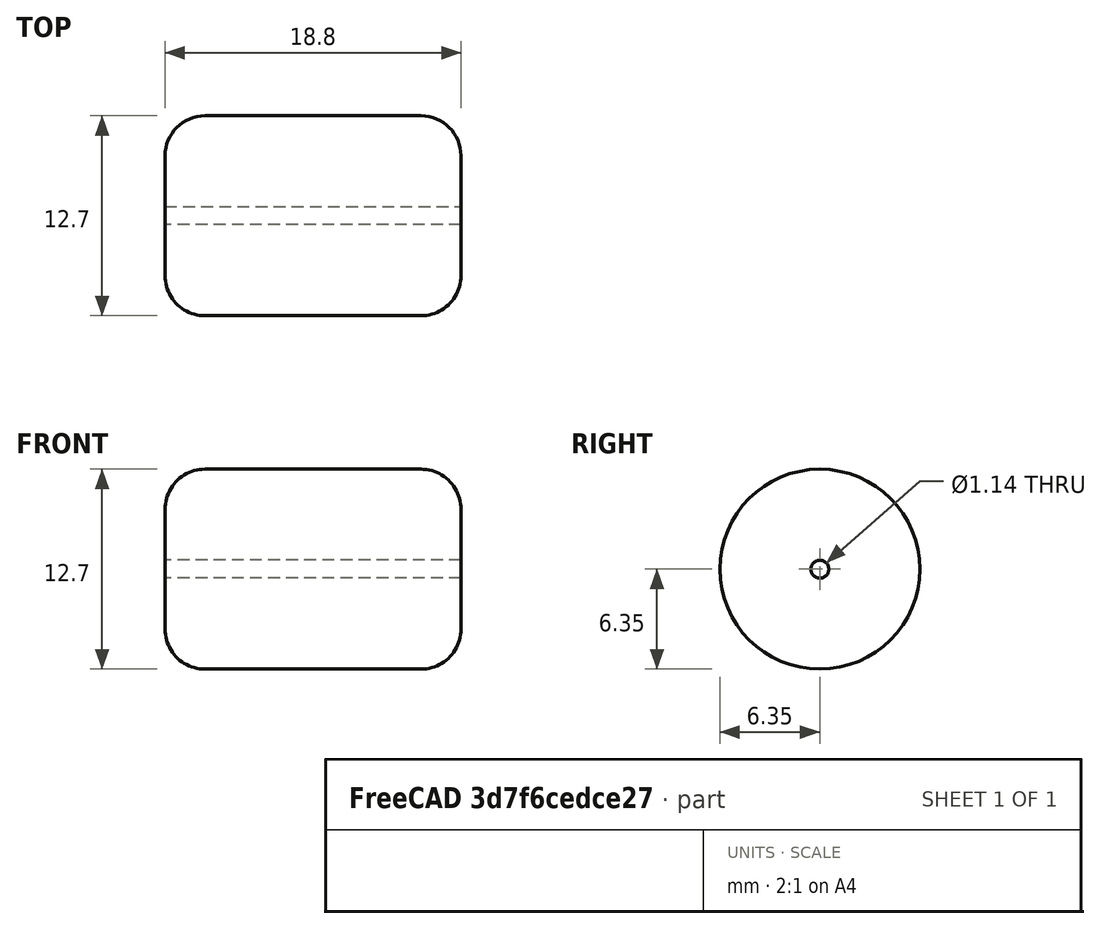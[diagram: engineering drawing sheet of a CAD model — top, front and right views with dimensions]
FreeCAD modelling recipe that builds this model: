
FCSTD DOCUMENT  (FreeCAD 0.20R27936 (Git))
Label: Idler Wheel
License: All rights reserved
LicenseURL: http://en.wikipedia.org/wiki/All_rights_reserved
objects: Sketcher::SketchObject×1, PartDesign::Pad×1, PartDesign::Fillet×1, PartDesign::Body×1
note: 6 computed .brp shape members not serialized (recipe doc carries the construction recipe); baked Part::Feature solids carry a one-line shape summary decoded from their .brp

FEATURE [Sketcher::SketchObject] Sketch
  FullyConstrained = true
  MapMode = 5
  Placement = pos=(0,0,0) rot=(0.57735,0.57735,0.57735;2.0944rad)
  Support = -> [YZ_Plane]
  sketch-geometry (2):
    g0: Circle CenterX=0 CenterY=0 CenterZ=0 NormalX=0 NormalY=0 NormalZ=1 AngleXU=0 Radius=6.35
    g1: Circle CenterX=0 CenterY=0 CenterZ=0 NormalX=0 NormalY=0 NormalZ=1 AngleXU=0 Radius=0.5715
  constraints (4):
    c: Coincident(g0,g-1)
    c: Diameter(g0) = 12.7
    c: Coincident(g1,g0)
    c: Diameter(g1) = 1.143
FEATURE [PartDesign::Pad] Pad
  Direction = (1,-2e-16,3e-16)
  Length = 18.796
  Length2 = 10.0076
  Placement = pos=(0,0,0) rot=(0.57735,0.57735,0.57735;2.0944rad)
  Profile = -> Sketch
  ReferenceAxis = -> Sketch [N_Axis]
  Type = 0
FEATURE [PartDesign::Fillet] Fillet
  Base = -> Pad [Edge3,Edge2]
  BaseFeature = -> Pad
  Placement = pos=(0,0,0) rot=(0.57735,0.57735,0.57735;2.0944rad)
  Radius = 2.54
  SupportTransform = false
  UseAllEdges = false
FEATURE [PartDesign::Body] Body  label="Idler Wheel"
  Group = -> [Sketch,Pad,Fillet]
  Origin = -> Origin
  Tip = -> Fillet
